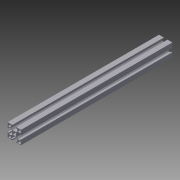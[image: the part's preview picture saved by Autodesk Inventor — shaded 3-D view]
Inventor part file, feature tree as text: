
AUTODESK INVENTOR PART (.ipt)
format: ipt  version: 2015 SP1 (Build 190203100, 203)  size: 208,896 bytes
history: native  units: mm (DEFAULTED — no unit token found)
features: other x12, extrude x1, sketch x1
ambient origin geometry x8: Origin, YZ Plane, XZ Plane, XY Plane, X Axis, Y Axis, Z Axis, Center Point
bodies: Solid1 (feature_tree)
feature tree (14):
  other  "Table"
  other  "20.1068-30X30-100"
  other  "20.1068-30X30-130"
  other  "20.1068-30X30-160"
  other  "20.1068-30X30-200"
  other  "20.1068-30X30-270"
  other  "20.1068-30X30-280"
  other  "20.1068-30X30-340"
  other  "20.1068-30X30-400"
  other  "20.1068-30X30-470"
  other  "20.1068-30X30-500"
  other  "20.1068-30X30-3-601"
  extrude  "Extrusion1"  [1 undecoded]
  sketch  "Sketch1"  dims[d3=0.0mm]
note: 1 required parameter value undecoded (feature->parameter linkage not recoverable at this tier; creation-order binding heuristic only, values carry confidence <= 0.55)
